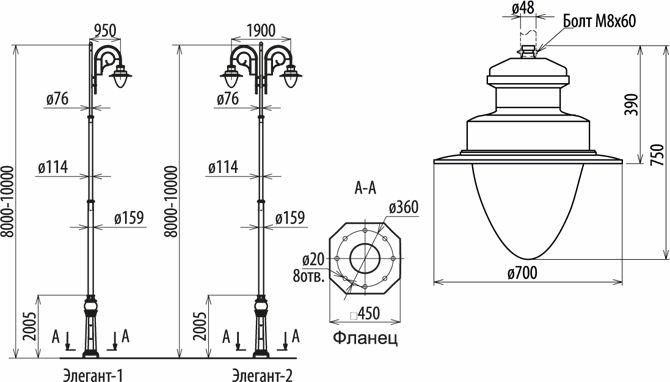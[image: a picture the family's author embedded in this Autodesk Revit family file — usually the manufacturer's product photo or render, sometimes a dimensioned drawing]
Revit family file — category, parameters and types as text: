
# Revit family: svetilnik_alfresco_elegant-1-8_i_1-10
name_source: partatom
category: Lighting Fixtures
revit_build: Autodesk Revit 2016 (Build: 20150506_1715(x64)
units: mm (PartAtom-declared; Revit-internal decimal feet)

## family parameters
Always vertical = Yes
Cut with Voids When Loaded = No
Light Source = No
Part Type = Normal
Room Calculation Point = No
Round Connector Dimension = Use Diameter
Shared = No
Work Plane-Based = No

## types (2) — shared parameters
ADSK_Единица измерения = шт
ADSK_Классификация нагрузок = Освещение
ADSK_Количество фаз = 2
ADSK_Количество фаз числовое = 2
ADSK_Коэффициент мощности = 0.97
ADSK_Модель = Элегант-1
ADSK_Напряжение = 220 V
ADSK_Размер_Длина = 950 mm  [stored 3.1168 ft]
ADSK_Размер_Ширина = 700 mm  [stored 2.29659 ft]
ADSK_Ток = 0 A
ADSK_Энергоэффективность = 120 lm/W
D = 159 mm  [stored 0.521654 ft]
D1 = 114 mm  [stored 0.374016 ft]
IP Class = IP 65
Manufacturer = ALFRESCO
R1 = 89.5 mm
URL = http://www.allfresco.ru
Блок аварийного питания = No
Класс Защиты = 1
Класс пожароопасности = F (светильники предназначены для установки непосредственно на поверхность из нормально воспламеняемых матеоиалов)
Климатическая зона = УХЛ1
Материал опоры = Сталь, окрашенная, черная
Область использования = ландшафт, коттедж.поселки,микрорайоны,АЗС, автостоянки
Температура эксплуатации = -35 +40
Тип ИС = LED-светодиоды
Тип КСС = Sym
Тип ПРА = -
Тип продукции = Комплект(Опора освещения+LED светильник)
Цветовая температура = 3000-5500

## per-type parameters (varying)
| type | ADSK_Артикул | ADSK_Масса | ADSK_Наименование | ADSK_Номинальная мощность | ADSK_Полная мощность | ADSK_Размер_Высота | Apparent Load | Световой поток | Тип светильника |
| Элегант-1-8,0 ДСУ 80Вт | 1147000130 | 314 | Элегант-1-8,0 ДСУ 80Вт - св-к Росинка II ДСУ-01-AF (120, 02) на опоре ORD 8,0-1-32 ЧМ | 80 W | 82 VA | 8000 mm  [stored 26.2467 ft] | 82 VA | 9600 lm | Элегант : Элегант 80Вт |
| Элегант-1-10,0 ДСУ 100Вт | 1147000140 | 337 | Элегант-1-10,0 ДСУ 100Вт - св-к Росинка II ДСУ-01-AF (120, 02) на опоре ORD 10,0-1-32 ЧМ | 100 W | 103 VA | 10000 mm  [stored 32.8084 ft] | 103 VA | 12000 lm | Элегант : Элегант 100Вт |

note: [stored X ft] marks values corroborated as IEEE doubles in the binary element streams (Revit-internal decimal feet)
